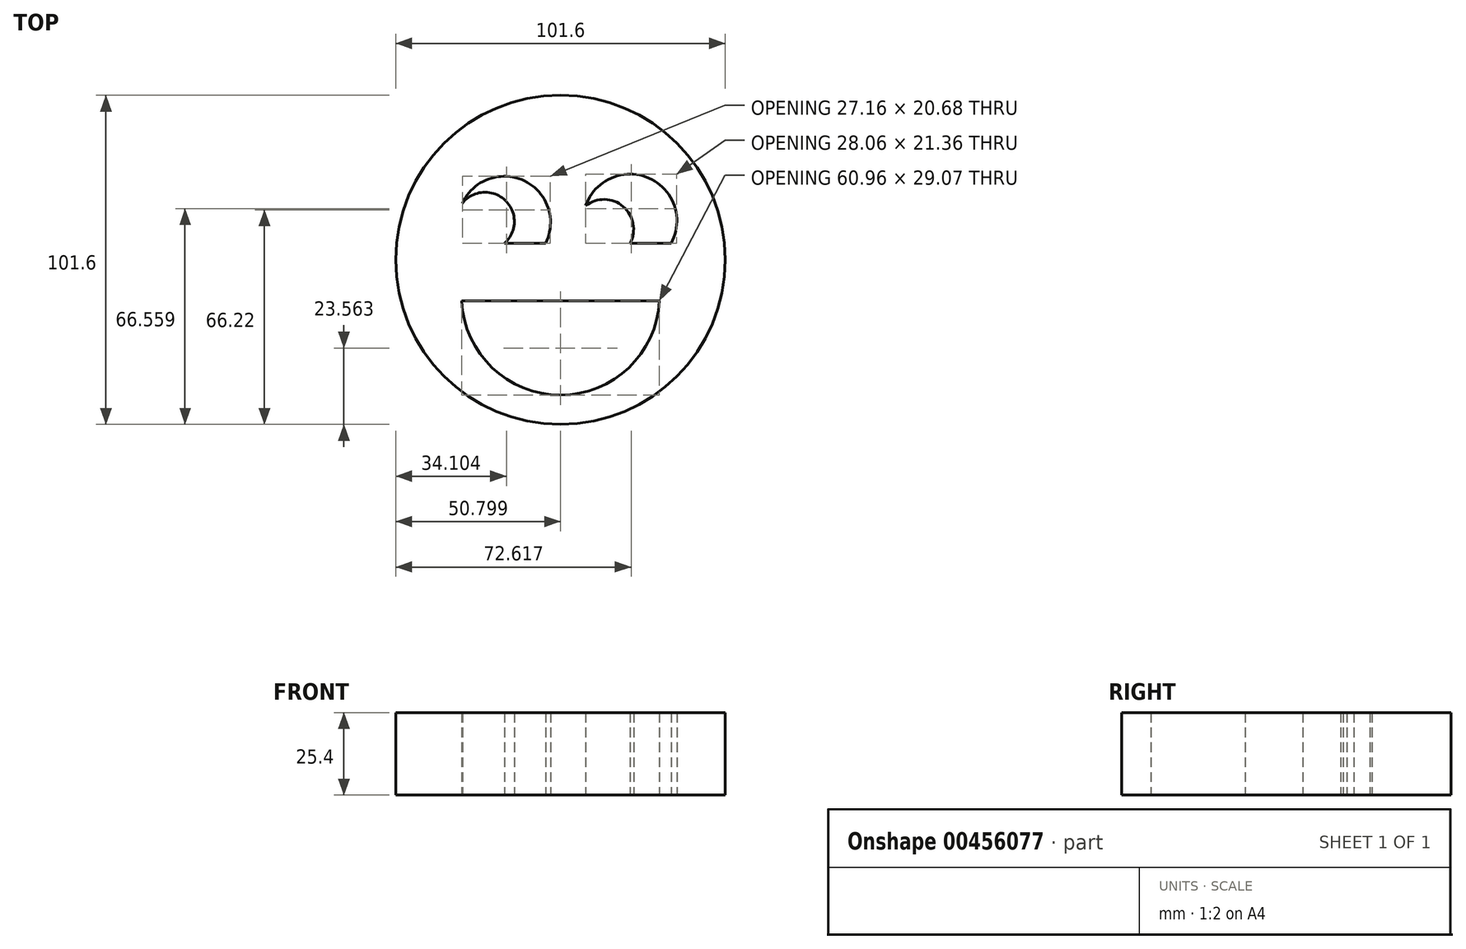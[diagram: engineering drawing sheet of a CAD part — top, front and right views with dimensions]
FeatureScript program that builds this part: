
annotation { "Feature Type Name" : "Feature", "Feature Type Description" : "" }
export const myFeature = defineFeature(function(context is Context, id is Id, definition is map)
    precondition{}
    {
        {
            var Q0;
            Q0=qCreatedBy(makeId("Top.planeOp"),FACE);
            var sketch = newSketch(context, id + "F0", { "sketchPlane" : qUnion([Q0])});
            skCircle(sketch, "E0", {"center": v(2.77, 0) * mm, "radius": 50.8 * mm});
            skLineSegment(sketch, "E1", {"start": v(-27.71, -12.7) * mm, "end": v(33.25, -12.7) * mm});
            skArc(sketch, "E2", {"start": v(-27.71, -12.7) * mm, "mid": v(2.77, -41.77) * mm, "end": v(33.25, -12.7) * mm});
            skLineSegment(sketch, "E3", {"start": v(-14.55, 5.08) * mm, "end": v(-1.85, 5.08) * mm});
            skLineSegment(sketch, "E4", {"start": v(24.21, 5.08) * mm, "end": v(36.91, 5.08) * mm});
            skArc(sketch, "E5", {"start": v(36.91, 5.08) * mm, "mid": v(30.05, 25.2) * mm, "end": v(10.56, 16.72) * mm});
            skArc(sketch, "E6", {"start": v(-1.85, 5.08) * mm, "mid": v(-8.36, 24.36) * mm, "end": v(-27.5, 17.46) * mm});
            skArc(sketch, "E7", {"start": v(-14.55, 5.08) * mm, "mid": v(-14.26, 18.36) * mm, "end": v(-27.5, 17.46) * mm});
            skArc(sketch, "E8", {"start": v(24.21, 5.08) * mm, "mid": v(22.1, 16.44) * mm, "end": v(10.56, 16.72) * mm});
            skPoint(sketch, "E9.orphan", {"position": v(-27.25, 5.08) * mm});
            skPoint(sketch, "E10.orphan", {"position": v(11.51, 5.08) * mm});
            skSolve(sketch);
        }
        {
            var Q0;
            Q0=makeQuery(id+"F0.imprint","IMPRINT",FACE,{"disambiguationData":[TD([[makeQuery(id+"F0.imprint","IMPRINT",EDGE,{"derivedFrom":sQuery(id+"F0.wireOp",EDGE,"E0")}),1.0]])]});
            extrude(context, id + "F1", {"entities" : qUnion([Q0]), "depth" : 25.4 * mm});
        }
    });
